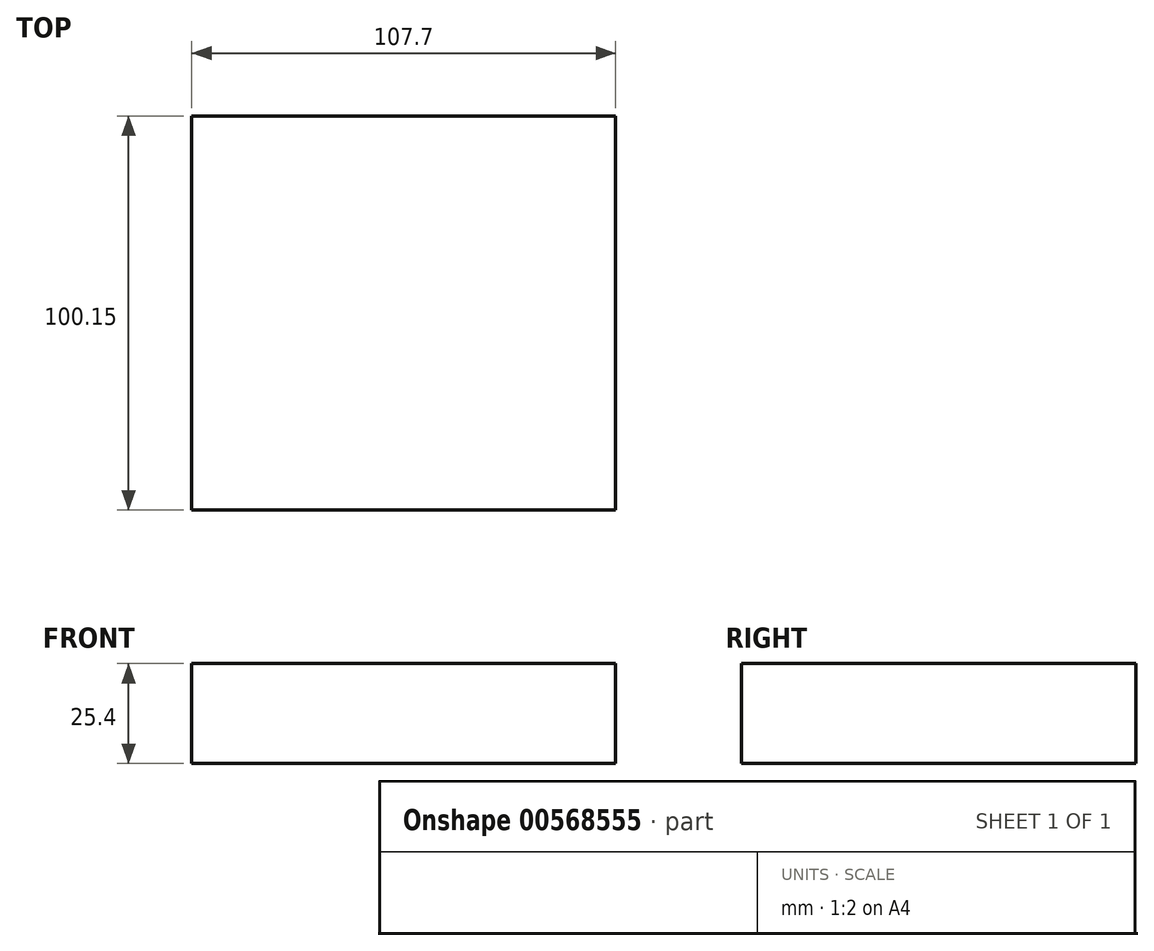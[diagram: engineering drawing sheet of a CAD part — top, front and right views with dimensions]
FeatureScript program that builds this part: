
annotation { "Feature Type Name" : "Feature", "Feature Type Description" : "" }
export const myFeature = defineFeature(function(context is Context, id is Id, definition is map)
    precondition{}
    {
        {
            var Q0;
            Q0=qCreatedBy(makeId("Top.planeOp"),FACE);
            var sketch = newSketch(context, id + "F0", { "sketchPlane" : qUnion([Q0])});
            skLineSegment(sketch, "E0.bottom", {"start": v(-144.71, 54.67) * mm, "end": v(-37, 54.67) * mm});
            skLineSegment(sketch, "E0.top", {"start": v(-144.71, -45.48) * mm, "end": v(-37, -45.48) * mm});
            skLineSegment(sketch, "E0.left", {"start": v(-144.71, 54.67) * mm, "end": v(-144.71, -45.48) * mm});
            skLineSegment(sketch, "E0.right", {"start": v(-37, 54.67) * mm, "end": v(-37, -45.48) * mm});
            skSolve(sketch);
        }
        {
            var Q0;
            Q0 = qSketchRegion(id + "F0", true);
            extrude(context, id + "F1", {"entities" : qUnion([Q0]), "depth" : 25.4 * mm, "offsetDistance" : 25.4 * mm});
        }
    });
